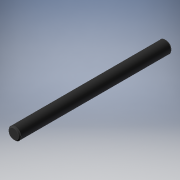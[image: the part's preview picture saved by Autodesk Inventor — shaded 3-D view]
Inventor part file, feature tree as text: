
AUTODESK INVENTOR PART (.ipt)
format: ipt  version: 2019 (Build 230136000, 136)  size: 113,152 bytes
history: native  units: mm
features: other x7, revolve x1, sketch x1
ambient origin geometry x8: Origin, YZ Plane, XZ Plane, XY Plane, X Axis, Y Axis, Z Axis, Center Point
bodies: Solid1 (feature_tree)
feature tree (9):
  revolve  "Revolution1"  [1 undecoded]
  other  "to_leaf_XY"
  other  "to_leaf_YZ"
  other  "to_leaf_ZX"
  other  "to_leaf_X"
  other  "to_leaf_Y"
  other  "to_leaf_Z"
  other  "to_leaf_Center"
  sketch  "Sketch_1"  dims[d0=360.0deg d1=0.0mm]
note: 1 required parameter value undecoded (feature->parameter linkage not recoverable at this tier; creation-order binding heuristic only, values carry confidence <= 0.55)
